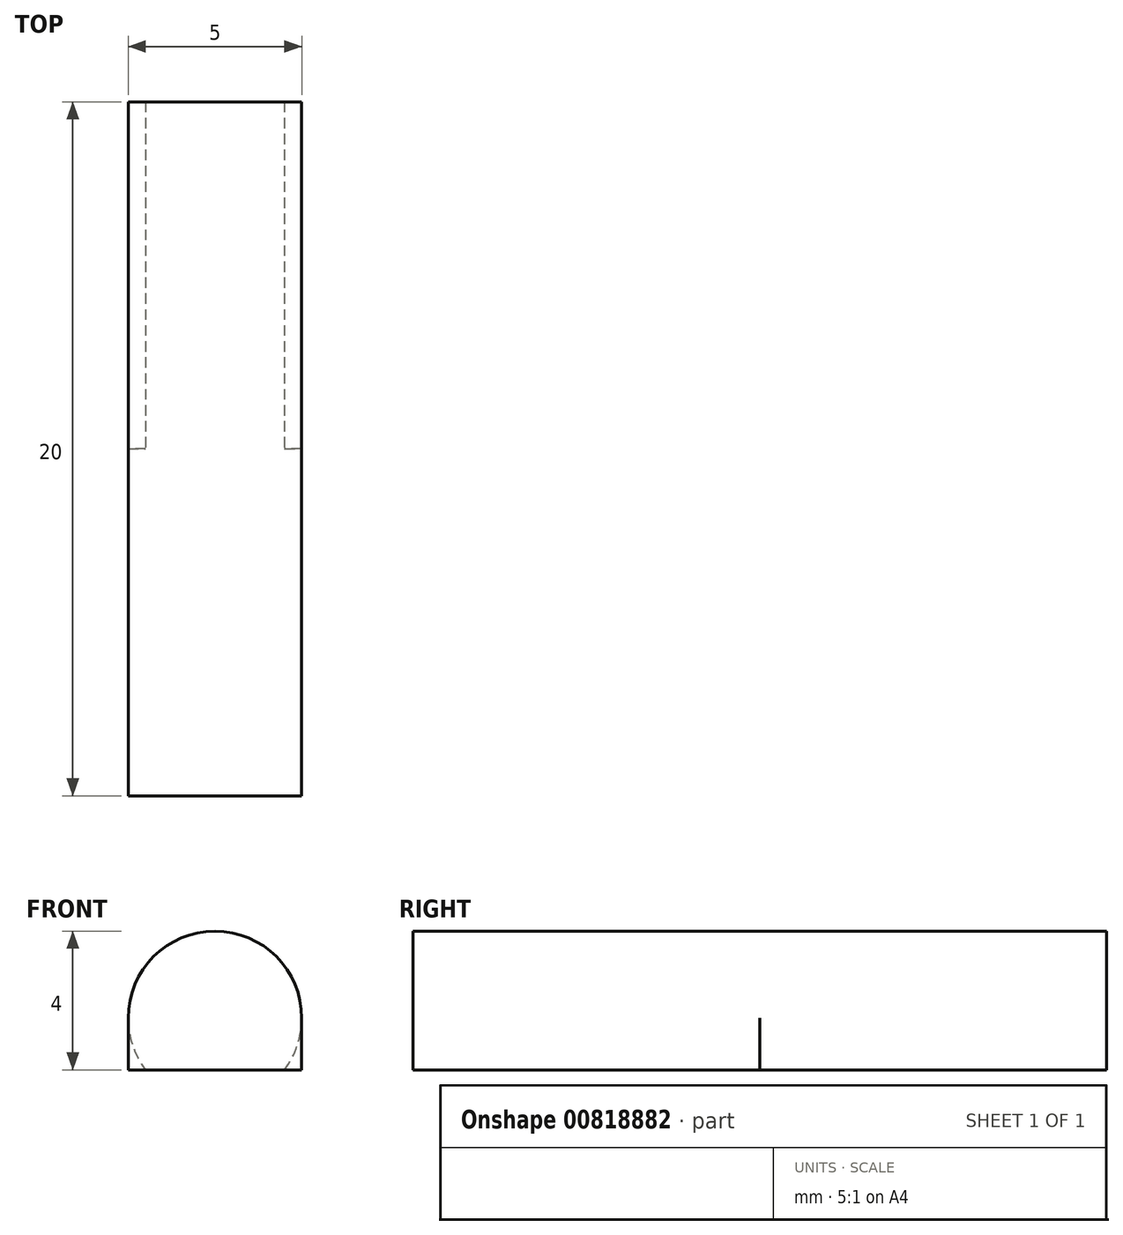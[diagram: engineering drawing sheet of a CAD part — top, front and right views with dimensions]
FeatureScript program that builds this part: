
annotation { "Feature Type Name" : "Feature", "Feature Type Description" : "" }
export const myFeature = defineFeature(function(context is Context, id is Id, definition is map)
    precondition{}
    {
        {
            var Q0;
            Q0=qCreatedBy(makeId("Front.planeOp"),FACE);
            var sketch = newSketch(context, id + "F0", { "sketchPlane" : qUnion([Q0])});
            skCircle(sketch, "E0", {"center": v(-22.1, 13.1) * mm, "radius": 2.5 * mm});
            skSolve(sketch);
        }
        {
            var Q0;
            Q0=makeQuery(id+"F0.imprint","IMPRINT",FACE,{"disambiguationData":[TD([[makeQuery(id+"F0.imprint","IMPRINT",EDGE,{"derivedFrom":sQuery(id+"F0.wireOp",EDGE,"E0")}),1.0]])]});
            extrude(context, id + "F1", {"entities" : qUnion([Q0]), "depth" : 10 * mm, "offsetDistance" : 25 * mm});
        }
        {
            var Q0;
            Q0=makeQuery(id+"F1.opExtrude","CAP_FACE",FACE,{"disambiguationData":[OSD([sQuery(id+"F0.wireOp",EDGE,"E0")])],"isStart":false});
            var sketch = newSketch(context, id + "F2", { "sketchPlane" : qUnion([Q0])});
            skLineSegment(sketch, "E1", {"start": v(-24.1, 11.6) * mm, "end": v(-20.1, 11.6) * mm});
            skLineSegment(sketch, "E2", {"start": v(-24.1, 14.6) * mm, "end": v(-20.1, 14.6) * mm});
            skSolve(sketch);
        }
        {
            var Q0;
            {var subQ0=sQuery(id+"F2.wireOp",EDGE,"E1");Q0=makeQuery(id+"F2.imprint","IMPRINT",FACE,{"disambiguationData":[TD([[makeQuery(id+"F2.imprint","IMPRINT",EDGE,{"derivedFrom":subQ0}),-1.0]])]});}
            extrude(context, id + "F3", {"entities" : qUnion([Q0]), "operationType" : NewBodyOperationType.REMOVE, "oppositeDirection" : true, "depth" : 10 * mm, "offsetDistance" : 25 * mm});
        }
        {
            var Q0;
            Q0=makeQuery(id+"F1.opExtrude","CAP_FACE",FACE,{"disambiguationData":[OSD([sQuery(id+"F0.wireOp",EDGE,"E0")])],"isStart":false});
            extrude(context, id + "F4", {"entities" : qUnion([Q0]), "operationType" : NewBodyOperationType.ADD, "depth" : 10 * mm, "offsetDistance" : 25 * mm});
        }
        {
            var Q0;
            {var subQ0=sQuery(id+"F2.wireOp",EDGE,"E1");Q0=makeQuery(id+"F4.boolean.opBoolean","MERGE",FACE,{"derivedFrom":[makeQuery(id+"F3.boolean.opBoolean","COPY",FACE,{"derivedFrom":makeQuery(id+"F3.opExtrude","SWEPT_FACE",FACE,{"disambiguationData":[OSD([subQ0])]})}),makeQuery(id+"F4.opExtrude","SWEPT_FACE",FACE,{"disambiguationData":[OSD([subQ0])]})]});}
            var sketch = newSketch(context, id + "F5", { "sketchPlane" : qUnion([Q0])});
            skLineSegment(sketch, "E3", {"start": v(-20.1, 10) * mm, "end": v(-24.1, 10) * mm});
            skPoint(sketch, "E4", {"position": v(-22.1, 10) * mm});
            skLineSegment(sketch, "E5.bottom", {"start": v(-20.1, 20) * mm, "end": v(-19.6, 20) * mm});
            skLineSegment(sketch, "E5.top", {"start": v(-20.1, 10) * mm, "end": v(-19.6, 10) * mm});
            skLineSegment(sketch, "E5.left", {"start": v(-20.1, 20) * mm, "end": v(-20.1, 10) * mm});
            skLineSegment(sketch, "E5.right", {"start": v(-19.6, 20) * mm, "end": v(-19.6, 10) * mm});
            skLineSegment(sketch, "E6.bottom", {"start": v(-24.1, 20) * mm, "end": v(-24.6, 20) * mm});
            skLineSegment(sketch, "E6.top", {"start": v(-24.1, 10) * mm, "end": v(-24.6, 10) * mm});
            skLineSegment(sketch, "E6.left", {"start": v(-24.1, 20) * mm, "end": v(-24.1, 10) * mm});
            skLineSegment(sketch, "E6.right", {"start": v(-24.6, 20) * mm, "end": v(-24.6, 10) * mm});
            skSolve(sketch);
        }
        {
            var Q0;
            Q0=makeQuery(id+"F5.imprint","IMPRINT",FACE,{"disambiguationData":[TD([[makeQuery(id+"F5.imprint","IMPRINT",EDGE,{"derivedFrom":sQuery(id+"F5.wireOp",EDGE,"E6.bottom")}),1.0]])]});
            var Q1;
            Q1=makeQuery(id+"F5.imprint","IMPRINT",FACE,{"disambiguationData":[TD([[makeQuery(id+"F5.imprint","IMPRINT",EDGE,{"derivedFrom":sQuery(id+"F5.wireOp",EDGE,"E5.bottom")}),-1.0]])]});
            extrude(context, id + "F6", {"entities" : qUnion([Q0, Q1]), "operationType" : NewBodyOperationType.ADD, "depth" : -1.5 * mm, "offsetDistance" : 25 * mm});
        }
    });
